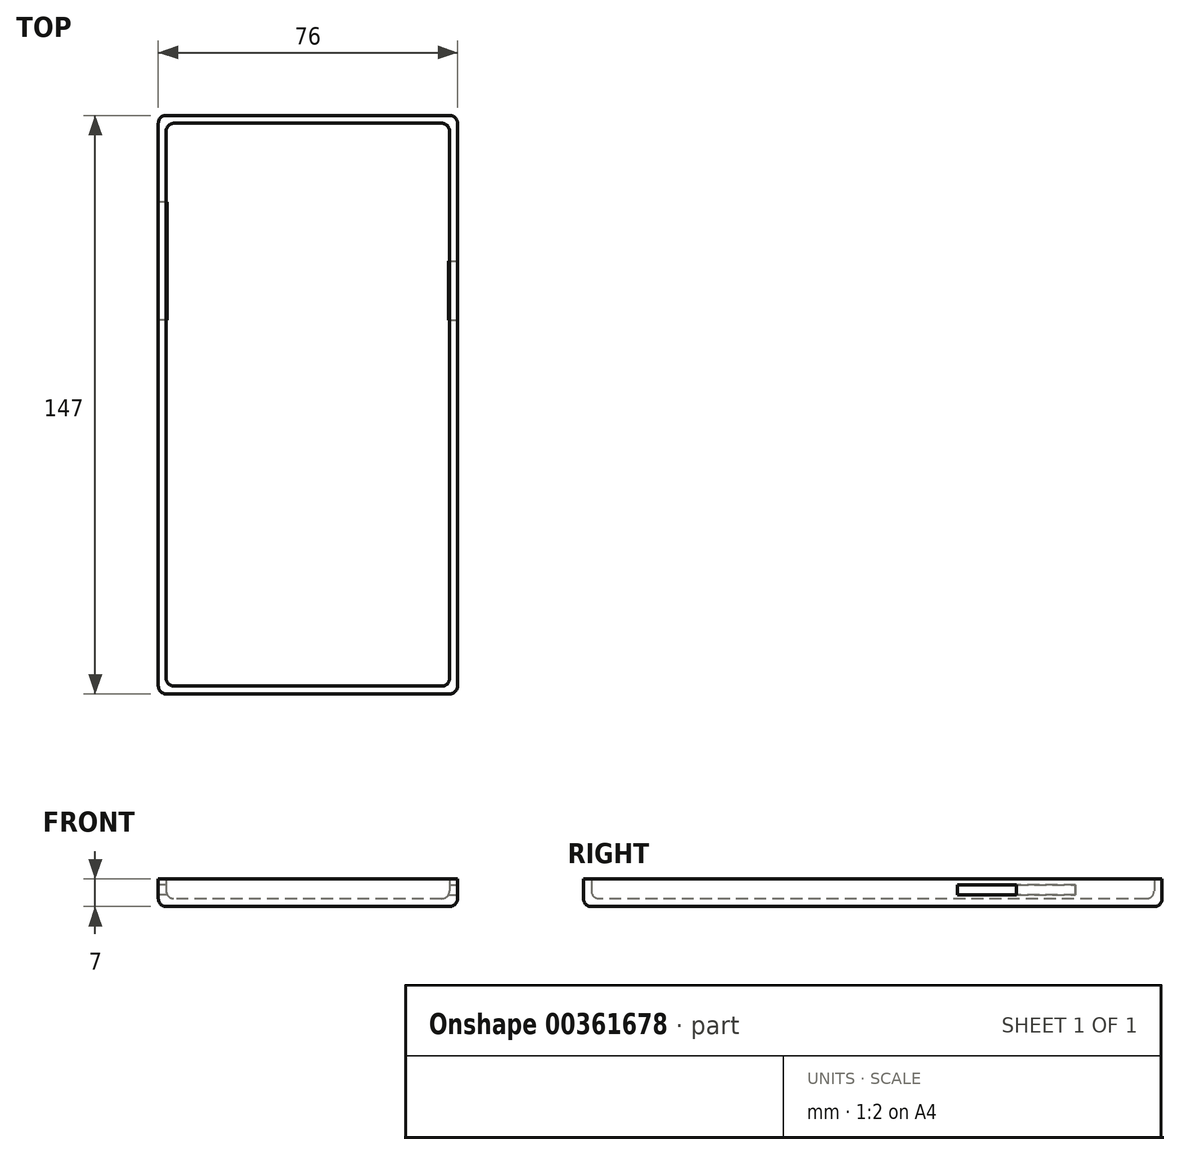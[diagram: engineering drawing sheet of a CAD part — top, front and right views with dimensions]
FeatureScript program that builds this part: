
annotation { "Feature Type Name" : "Feature", "Feature Type Description" : "" }
export const myFeature = defineFeature(function(context is Context, id is Id, definition is map)
    precondition{}
    {
        {
            var Q0;
            Q0=qCreatedBy(makeId("Top.planeOp"),FACE);
            var sketch = newSketch(context, id + "F0", { "sketchPlane" : qUnion([Q0])});
            skLineSegment(sketch, "E0.bottom", {"start": v(0, 0) * mm, "end": v(72, 0) * mm});
            skLineSegment(sketch, "E0.top", {"start": v(0, 143) * mm, "end": v(72, 143) * mm});
            skLineSegment(sketch, "E0.left", {"start": v(0, 0) * mm, "end": v(0, 143) * mm});
            skLineSegment(sketch, "E0.right", {"start": v(72, 0) * mm, "end": v(72, 143) * mm});
            skLineSegment(sketch, "E1.bottom", {"start": v(-2, 145) * mm, "end": v(74, 145) * mm});
            skLineSegment(sketch, "E1.top", {"start": v(-2, -2) * mm, "end": v(74, -2) * mm});
            skLineSegment(sketch, "E1.left", {"start": v(-2, 145) * mm, "end": v(-2, -2) * mm});
            skLineSegment(sketch, "E1.right", {"start": v(74, 145) * mm, "end": v(74, -2) * mm});
            skSolve(sketch);
        }
        {
            var Q0;
            Q0=makeQuery(id+"F0.imprint","IMPRINT",FACE,{"disambiguationData":[TD([[makeQuery(id+"F0.imprint","IMPRINT",EDGE,{"derivedFrom":sQuery(id+"F0.wireOp",EDGE,"E0.bottom")}),1.0]])]});
            var Q1;
            Q1=makeQuery(id+"F0.imprint","IMPRINT",FACE,{"disambiguationData":[TD([[makeQuery(id+"F0.imprint","IMPRINT",EDGE,{"derivedFrom":sQuery(id+"F0.wireOp",EDGE,"E0.bottom")}),-1.0]])]});
            extrude(context, id + "F1", {"entities" : qUnion([Q0, Q1]), "depth" : 2 * mm});
        }
        {
            var Q0;
            Q0=makeQuery(id+"F1.opExtrude","CAP_FACE",FACE,{"disambiguationData":[OSD([sQuery(id+"F0.wireOp",EDGE,"E1.bottom"),sQuery(id+"F0.wireOp",EDGE,"E1.top"),sQuery(id+"F0.wireOp",EDGE,"E1.left"),sQuery(id+"F0.wireOp",EDGE,"E1.right")])],"isStart":false});
            var sketch = newSketch(context, id + "F2", { "sketchPlane" : qUnion([Q0])});
            skLineSegment(sketch, "E2.bottom", {"start": v(-2, -2) * mm, "end": v(74, -2) * mm});
            skLineSegment(sketch, "E2.top", {"start": v(-2, 145) * mm, "end": v(74, 145) * mm});
            skLineSegment(sketch, "E2.left", {"start": v(-2, -2) * mm, "end": v(-2, 145) * mm});
            skLineSegment(sketch, "E2.right", {"start": v(74, -2) * mm, "end": v(74, 145) * mm});
            skLineSegment(sketch, "E3.bottom", {"start": v(72, 143) * mm, "end": v(0, 143) * mm});
            skLineSegment(sketch, "E3.top", {"start": v(72, 0) * mm, "end": v(0, 0) * mm});
            skLineSegment(sketch, "E3.left", {"start": v(72, 143) * mm, "end": v(72, 0) * mm});
            skLineSegment(sketch, "E3.right", {"start": v(0, 143) * mm, "end": v(0, 0) * mm});
            skSolve(sketch);
        }
        {
            var Q0;
            Q0 = qSketchRegion(id + "F2", true);
            extrude(context, id + "F3", {"entities" : qUnion([Q0]), "operationType" : NewBodyOperationType.ADD, "depth" : 5 * mm});
        }
        {
            var Q0;
            Q0=makeQuery(id+"F1.opExtrude","CAP_FACE",FACE,{"disambiguationData":[OSD([sQuery(id+"F0.wireOp",EDGE,"E1.bottom"),sQuery(id+"F0.wireOp",EDGE,"E1.top"),sQuery(id+"F0.wireOp",EDGE,"E1.left"),sQuery(id+"F0.wireOp",EDGE,"E1.right")])],"isStart":false});
            var Q1;
            Q1=makeQuery(id+"F1.opExtrude","CAP_FACE",FACE,{"disambiguationData":[OSD([sQuery(id+"F0.wireOp",EDGE,"E1.bottom"),sQuery(id+"F0.wireOp",EDGE,"E1.top"),sQuery(id+"F0.wireOp",EDGE,"E1.left"),sQuery(id+"F0.wireOp",EDGE,"E1.right")])],"isStart":true});
            var Q2;
            Q2=makeQuery(id+"F3.boolean.opBoolean","MERGE",EDGE,{"derivedFrom":[makeQuery(id+"F1.opExtrude","SWEPT_EDGE",EDGE,{"disambiguationData":[OSD([sQuery(id+"F0.wireOp",EDGE,"E1.top"),sQuery(id+"F0.wireOp",EDGE,"E1.right")])]}),makeQuery(id+"F3.opExtrude","SWEPT_EDGE",EDGE,{"disambiguationData":[OSD([sQuery(id+"F2.wireOp",EDGE,"E2.bottom"),sQuery(id+"F2.wireOp",EDGE,"E2.right")])]})]});
            var Q3;
            Q3=makeQuery(id+"F3.boolean.opBoolean","MERGE",EDGE,{"derivedFrom":[makeQuery(id+"F1.opExtrude","SWEPT_EDGE",EDGE,{"disambiguationData":[OSD([sQuery(id+"F0.wireOp",EDGE,"E1.top"),sQuery(id+"F0.wireOp",EDGE,"E1.left")])]}),makeQuery(id+"F3.opExtrude","SWEPT_EDGE",EDGE,{"disambiguationData":[OSD([sQuery(id+"F2.wireOp",EDGE,"E2.bottom"),sQuery(id+"F2.wireOp",EDGE,"E2.left")])]})]});
            var Q4;
            Q4=makeQuery(id+"F3.boolean.opBoolean","MERGE",EDGE,{"derivedFrom":[makeQuery(id+"F1.opExtrude","SWEPT_EDGE",EDGE,{"disambiguationData":[OSD([sQuery(id+"F0.wireOp",EDGE,"E1.bottom"),sQuery(id+"F0.wireOp",EDGE,"E1.left")])]}),makeQuery(id+"F3.opExtrude","SWEPT_EDGE",EDGE,{"disambiguationData":[OSD([sQuery(id+"F2.wireOp",EDGE,"E2.top"),sQuery(id+"F2.wireOp",EDGE,"E2.left")])]})]});
            var Q5;
            Q5=makeQuery(id+"F3.boolean.opBoolean","MERGE",EDGE,{"derivedFrom":[makeQuery(id+"F1.opExtrude","SWEPT_EDGE",EDGE,{"disambiguationData":[OSD([sQuery(id+"F0.wireOp",EDGE,"E1.bottom"),sQuery(id+"F0.wireOp",EDGE,"E1.right")])]}),makeQuery(id+"F3.opExtrude","SWEPT_EDGE",EDGE,{"disambiguationData":[OSD([sQuery(id+"F2.wireOp",EDGE,"E2.top"),sQuery(id+"F2.wireOp",EDGE,"E2.right")])]})]});
            var Q6;
            Q6=makeQuery(id+"F3.opExtrude","SWEPT_EDGE",EDGE,{"disambiguationData":[OSD([sQuery(id+"F2.wireOp",EDGE,"E3.top"),sQuery(id+"F2.wireOp",EDGE,"E3.left")])]});
            var Q7;
            Q7=makeQuery(id+"F3.opExtrude","SWEPT_EDGE",EDGE,{"disambiguationData":[OSD([sQuery(id+"F2.wireOp",EDGE,"E3.top"),sQuery(id+"F2.wireOp",EDGE,"E3.right")])]});
            var Q8;
            Q8=makeQuery(id+"F3.opExtrude","SWEPT_EDGE",EDGE,{"disambiguationData":[OSD([sQuery(id+"F2.wireOp",EDGE,"E3.bottom"),sQuery(id+"F2.wireOp",EDGE,"E3.right")])]});
            var Q9;
            Q9=makeQuery(id+"F3.opExtrude","SWEPT_EDGE",EDGE,{"disambiguationData":[OSD([sQuery(id+"F2.wireOp",EDGE,"E3.bottom"),sQuery(id+"F2.wireOp",EDGE,"E3.left")])]});
            fillet(context, id + "F4", {"entities" : qUnion([Q0, Q1, Q2, Q3, Q4, Q5, Q6, Q7, Q8, Q9]), "radius" : 2 * mm, "tangentPropagation" : true, "allowEdgeOverflow" : false});
        }
        {
            var Q0;
            Q0=makeQuery(id+"F3.boolean.opBoolean","MERGE",FACE,{"derivedFrom":[makeQuery(id+"F1.opExtrude","SWEPT_FACE",FACE,{"disambiguationData":[OSD([sQuery(id+"F0.wireOp",EDGE,"E1.right")])]}),makeQuery(id+"F3.opExtrude","SWEPT_FACE",FACE,{"disambiguationData":[OSD([sQuery(id+"F2.wireOp",EDGE,"E2.right")])]})]});
            var sketch = newSketch(context, id + "F5", { "sketchPlane" : qUnion([Q0])});
            skLineSegment(sketch, "E4.bottom", {"start": v(108, 5.5) * mm, "end": v(93, 5.5) * mm});
            skLineSegment(sketch, "E4.top", {"start": v(108, 3) * mm, "end": v(93, 3) * mm});
            skLineSegment(sketch, "E4.left", {"start": v(108, 5.5) * mm, "end": v(108, 3) * mm});
            skLineSegment(sketch, "E4.right", {"start": v(93, 5.5) * mm, "end": v(93, 3) * mm});
            skSolve(sketch);
        }
        {
            var Q0;
            Q0 = qSketchRegion(id + "F5", true);
            extrude(context, id + "F6", {"entities" : qUnion([Q0]), "operationType" : NewBodyOperationType.REMOVE, "oppositeDirection" : true, "depth" : 5 * mm});
        }
        {
            var Q0;
            Q0=makeQuery(id+"F3.boolean.opBoolean","MERGE",FACE,{"derivedFrom":[makeQuery(id+"F1.opExtrude","SWEPT_FACE",FACE,{"disambiguationData":[OSD([sQuery(id+"F0.wireOp",EDGE,"E1.left")])]}),makeQuery(id+"F3.opExtrude","SWEPT_FACE",FACE,{"disambiguationData":[OSD([sQuery(id+"F2.wireOp",EDGE,"E2.left")])]})]});
            var sketch = newSketch(context, id + "F7", { "sketchPlane" : qUnion([Q0])});
            skLineSegment(sketch, "E5.bottom", {"start": v(-123, 3) * mm, "end": v(-93, 3) * mm});
            skLineSegment(sketch, "E5.top", {"start": v(-123, 5.5) * mm, "end": v(-93, 5.5) * mm});
            skLineSegment(sketch, "E5.left", {"start": v(-123, 3) * mm, "end": v(-123, 5.5) * mm});
            skLineSegment(sketch, "E5.right", {"start": v(-93, 3) * mm, "end": v(-93, 5.5) * mm});
            skSolve(sketch);
        }
        {
            var Q0;
            Q0 = qSketchRegion(id + "F7", true);
            extrude(context, id + "F8", {"entities" : qUnion([Q0]), "operationType" : NewBodyOperationType.REMOVE, "oppositeDirection" : true, "depth" : 25 * mm});
        }
    });
